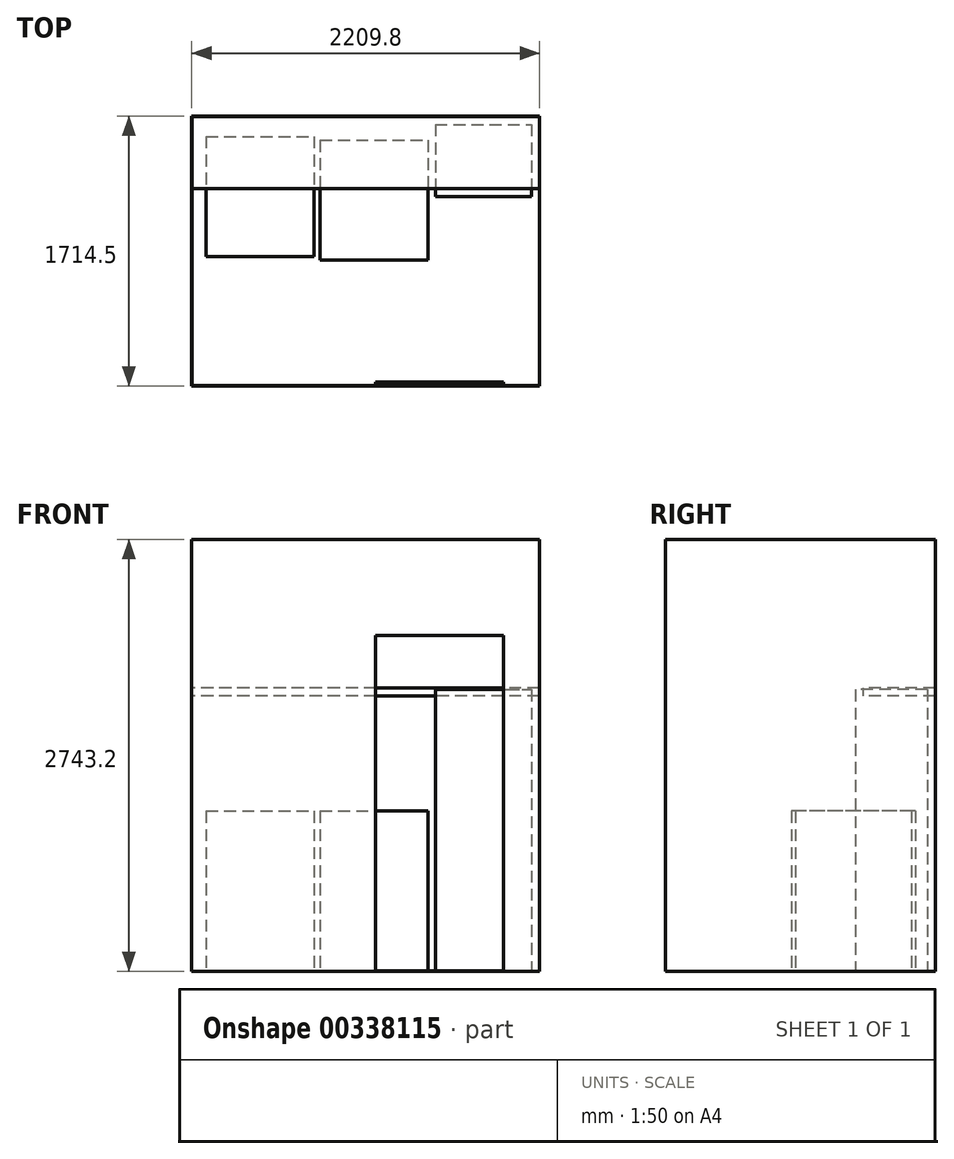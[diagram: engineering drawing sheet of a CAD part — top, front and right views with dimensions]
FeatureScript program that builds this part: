
annotation { "Feature Type Name" : "Feature", "Feature Type Description" : "" }
export const myFeature = defineFeature(function(context is Context, id is Id, definition is map)
    precondition{}
    {
        {
            var Q0;
            Q0=qCreatedBy(makeId("Top.planeOp"),FACE);
            var sketch = newSketch(context, id + "F0", { "sketchPlane" : qUnion([Q0])});
            skLineSegment(sketch, "E0.bottom", {"start": v(0, 0) * mm, "end": v(2209.8, 0) * mm});
            skLineSegment(sketch, "E0.top", {"start": v(0, 1714.5) * mm, "end": v(2209.8, 1714.5) * mm});
            skLineSegment(sketch, "E0.left", {"start": v(0, 0) * mm, "end": v(0, 1714.5) * mm});
            skLineSegment(sketch, "E0.right", {"start": v(2209.8, 0) * mm, "end": v(2209.8, 1714.5) * mm});
            skSolve(sketch);
        }
        {
            var Q0;
            Q0 = qSketchRegion(id + "F0", true);
            extrude(context, id + "F1", {"entities" : qUnion([Q0]), "depth" : 2743.2 * mm});
        }
        {
            var Q0;
            Q0=makeQuery(id+"F1.opExtrude","CAP_FACE",FACE,{"disambiguationData":[OSD([sQuery(id+"F0.wireOp",EDGE,"E0.bottom"),sQuery(id+"F0.wireOp",EDGE,"E0.top"),sQuery(id+"F0.wireOp",EDGE,"E0.left"),sQuery(id+"F0.wireOp",EDGE,"E0.right")])],"isStart":false});
            shell(context, id + "F2", {"entities" : qUnion([Q0]), "thickness" : 2.54 * mm});
        }
        {
            var Q0;
            Q0=makeQuery(id+"F1.opExtrude","SWEPT_FACE",FACE,{"disambiguationData":[OSD([sQuery(id+"F0.wireOp",EDGE,"E0.bottom")])]});
            var sketch = newSketch(context, id + "F3", { "sketchPlane" : qUnion([Q0])});
            skLineSegment(sketch, "E1.bottom", {"start": v(1168.4, 0) * mm, "end": v(1981.2, 0) * mm});
            skLineSegment(sketch, "E1.top", {"start": v(1168.4, 2133.6) * mm, "end": v(1981.2, 2133.6) * mm});
            skLineSegment(sketch, "E1.left", {"start": v(1168.4, 0) * mm, "end": v(1168.4, 2133.6) * mm});
            skLineSegment(sketch, "E1.right", {"start": v(1981.2, 0) * mm, "end": v(1981.2, 2133.6) * mm});
            skSolve(sketch);
        }
        {
            var Q0;
            Q0 = qSketchRegion(id + "F3", true);
            extrude(context, id + "F4", {"entities" : qUnion([Q0]), "operationType" : NewBodyOperationType.REMOVE, "oppositeDirection" : true, "depth" : 25.4 * mm});
        }
        {
            var Q0;
            Q0=makeQuery(id+"F2.opShell","OFFSET_FACE",FACE,{"disambiguationData":[OSD([sQuery(id+"F0.wireOp",EDGE,"E0.bottom"),sQuery(id+"F0.wireOp",EDGE,"E0.top"),sQuery(id+"F0.wireOp",EDGE,"E0.left"),sQuery(id+"F0.wireOp",EDGE,"E0.right")])]});
            var sketch = newSketch(context, id + "F5", { "sketchPlane" : qUnion([Q0])});
            skLineSegment(sketch, "E2.bottom", {"start": v(91.44, 1584.96) * mm, "end": v(777.24, 1584.96) * mm});
            skLineSegment(sketch, "E2.top", {"start": v(91.44, 822.96) * mm, "end": v(777.24, 822.96) * mm});
            skLineSegment(sketch, "E2.left", {"start": v(91.44, 1584.96) * mm, "end": v(91.44, 822.96) * mm});
            skLineSegment(sketch, "E2.right", {"start": v(777.24, 1584.96) * mm, "end": v(777.24, 822.96) * mm});
            skLineSegment(sketch, "E3.bottom", {"start": v(815.34, 1562.1) * mm, "end": v(1501.14, 1562.1) * mm});
            skLineSegment(sketch, "E3.top", {"start": v(815.34, 800.1) * mm, "end": v(1501.14, 800.1) * mm});
            skLineSegment(sketch, "E3.left", {"start": v(815.34, 1562.1) * mm, "end": v(815.34, 800.1) * mm});
            skLineSegment(sketch, "E3.right", {"start": v(1501.14, 1562.1) * mm, "end": v(1501.14, 800.1) * mm});
            skSolve(sketch);
        }
        {
            var Q0;
            Q0 = qSketchRegion(id + "F5", true);
            extrude(context, id + "F6", {"entities" : qUnion([Q0]), "depth" : 1016 * mm});
        }
        {
            var Q0;
            Q0=makeQuery(id+"F2.opShell","OFFSET_FACE",FACE,{"disambiguationData":[OSD([sQuery(id+"F0.wireOp",EDGE,"E0.left")])]});
            var sketch = newSketch(context, id + "F7", { "sketchPlane" : qUnion([Q0])});
            skLineSegment(sketch, "E4.bottom", {"start": v(1254.76, 1799.6) * mm, "end": v(1711.96, 1799.6) * mm});
            skLineSegment(sketch, "E4.top", {"start": v(1254.76, 1748.8) * mm, "end": v(1711.96, 1748.8) * mm});
            skLineSegment(sketch, "E4.left", {"start": v(1254.76, 1799.6) * mm, "end": v(1254.76, 1748.8) * mm});
            skLineSegment(sketch, "E4.right", {"start": v(1711.96, 1799.6) * mm, "end": v(1711.96, 1748.8) * mm});
            skSolve(sketch);
        }
        {
            var Q0;
            Q0 = qSketchRegion(id + "F7", true);
            var Q1;
            Q1=makeQuery(id+"F2.opShell","OFFSET_FACE",FACE,{"disambiguationData":[OSD([sQuery(id+"F0.wireOp",EDGE,"E0.right")])]});
            extrude(context, id + "F8", {"entities" : qUnion([Q0]), "endBound" : BoundingType.UP_TO_SURFACE, "endBoundEntityFace" : qUnion([Q1]), "depth" : 25.4 * mm});
        }
        {
            var Q0;
            Q0=makeQuery(id+"F2.opShell","OFFSET_FACE",FACE,{"disambiguationData":[OSD([sQuery(id+"F0.wireOp",EDGE,"E0.bottom"),sQuery(id+"F0.wireOp",EDGE,"E0.top"),sQuery(id+"F0.wireOp",EDGE,"E0.left"),sQuery(id+"F0.wireOp",EDGE,"E0.right")])]});
            var sketch = newSketch(context, id + "F9", { "sketchPlane" : qUnion([Q0])});
            skLineSegment(sketch, "E5.bottom", {"start": v(1546.86, 1661.16) * mm, "end": v(2156.46, 1661.16) * mm});
            skLineSegment(sketch, "E5.top", {"start": v(1546.86, 1203.96) * mm, "end": v(2156.46, 1203.96) * mm});
            skLineSegment(sketch, "E5.left", {"start": v(1546.86, 1661.16) * mm, "end": v(1546.86, 1203.96) * mm});
            skLineSegment(sketch, "E5.right", {"start": v(2156.46, 1661.16) * mm, "end": v(2156.46, 1203.96) * mm});
            skSolve(sketch);
        }
        {
            var Q0;
            Q0 = qSketchRegion(id + "F9", true);
            extrude(context, id + "F10", {"entities" : qUnion([Q0]), "depth" : 1787.52 * mm});
        }
    });
